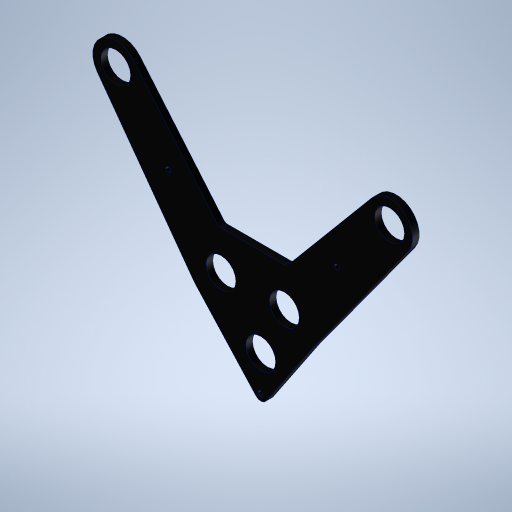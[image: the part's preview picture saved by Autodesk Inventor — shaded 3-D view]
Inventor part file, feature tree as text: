
AUTODESK INVENTOR PART (.ipt)
format: ipt  version: 2024 (Build 280153000, 153)  size: 314,880 bytes
history: native  units: in
note: dims shown in document units (in); Inventor stores cm internally (conversion verified against a paired STEP export)
features: extrude x1, sketch x1
ambient origin geometry x8: Origin, YZ Plane, XZ Plane, XY Plane, X Axis, Y Axis, Z Axis, Center Point
bodies: Solid1 (feature_tree)
feature tree (2):
  extrude  "Extrusion1"  Depth=0.25in
  sketch  "Sketch1"  dims[d0=1.8in d1=2.4in d2=0.1in d3=0.1in d4=0.125in d5=1.125in d6=1.654in d7=1.504in d14=1.75in d15=1.75in d16=0.1875in d17=0.1667in d18=0.196in d19=0.196in d20=0.5in d21=0.5in d23=0.0625in d24=6.209in d25=4.0in d26=4.0in d27=0.25in d28=0.0in]
